# Revit family: QF_ELECTROLUXPROFESSIONAL_1LSNTD_WS6-11_E
name_source: partatom
category: Attrezzature speciali
units: mm (PartAtom-declared; Revit-internal decimal feet)

## family parameters
Basato su piano di lavoro = No
Condiviso = No
Punto di calcolo locali = No
Quota connettore circolare = Usa diametro
Sempre verticale = Sì
Taglio con vuoti quando caricato = No
Tipo di parte = Normale

## types (17) — shared parameters
Depth = 697 mm  [stored 2.28675 ft]
Depth Actual = 700 mm  [stored 2.29659 ft]
Height = 1218.8 mm  [stored 3.99869 ft]
Height Actual = 1220 mm  [stored 4.00262 ft]
Latent Heat Output = 0.0
Length Actual = 720 mm  [stored 2.3622 ft]
Modello = WS6-11
Produttore = Electrolux Professional
Sensible Heat Output = 0.0
URL = www.electroluxprofessional.com
Weight = 152
Width = 720 mm  [stored 2.3622 ft]
zero-valued in all types: Gas KW, Prospetto di default, Steam Pounds per Hour

## per-type parameters (varying)
| type | Cycle | Descrizione | Item Number | Phase | Volts | Watts |
| 9867730227 | 50 Hz | WASHER WS6-11 11KG EL 10KW 380-415/50/3 COMPASS PRO 6G07 ML 2xWATER POWDER+5xLIQ. VALV.OPEN SST/SILVER 2.I/O QC TRAFO DI | 1L0H2N | 3 | 415 V | 8800 W |
| 9867730113 | 50 Hz | WASHER WS6-11 11KG MOP 10KW 380-415/50/3N COMPASS PRO 6F01 ML 2xWATER POWDER+ED EL.VALV.OPEN SST DISCON. STOP LID | 1L0GCV | 3 | 415 V | 8800 W |
| 9867730064 | 50 Hz | WASHER WS6-11 11KG EL 10KW 380-415/50/3N COMPASS PRO 6H01 ML 2xWATER POWDER+5xLIQ. VALV.OPEN SILVER 2.I/O DISCON. STOP | 1LSP5E | 3 | 415 V | 10400 W |
| 9867730112 | 50 Hz | WASHER WS6-11 11KG EL 10KW 380-415/50/3N COMPASS PRO 6G01 ML 2xWATER POWDER+5xLIQ. VALV.OPEN SILVER 2.I/O DISCON. STOP | 1L0GCU | 3 | 415 V | 8800 W |
| 9867730101 | 50 Hz | WASHER WS6-11 11KG NO HEAT 220-240/50/1N COMPASS PRO 6G05 ML 2xWATER POWDER+5xLIQ. VALV.OPEN SST/SILVER 2.I/O DISCON. ST | 1L821N | 1 | 240 V | 800 W |
| 9867730196 | 50 Hz | WASHER WS6-11 11KG NO HEAT 200/50/60/3 COMPASS PRO 6L41 JP,EN 2xWATER 5xLIQ. VALV.OPEN SST/SILVER 2.I/O DISCON. | 1L0GXM | 3 | 200 V | 900 W |
| 9867730122 | 50 Hz | WASHER WS6-11 11KG MOP 10KW 380-400/220-230/50/3N/3 COMPASS PRO 6M14 ML 2xWATER POWDER+5xLIQ. EL.VALV.OPEN SILVER 2.I/O | 1LA1CA | 3 | 415 V | 10400 W |
| 9867730082 | 50 Hz | WASHER WS6-11 11KG NO HEAT 220-240/50/1N COMPASS PRO 6L01 ML 2xWATER POWDER+5xLIQ. VALV.OPEN SILVER EXT.PM. 2.I/O DISCON | 1LSP5M | 1 | 240 V | 800 W |
| 9867730145 | 60 Hz | WASHER WS6-11 11KG EL 10KW 220-230/60/1 COMPASS PRO 6G07 ML 2xWATER POWDER+5xLIQ. VALV.OPEN SST 2.I/O QC DISCON. STOP | 1LSPD4 | 1 | 240 V | 10400 W |
| 9867730165 | 60 Hz | WASHER WS6-11 11KG NO HEAT 208-240/60/1 COMPASS PRO 6L01 ML 2xWATER POWDER+5xLIQ. VALV.OPEN SILVER ELS-NETW. 2.I/O | 1L0GNC | 1 | 240 V | 800 W |
| 9867730176 | 50 Hz | WASHER WS6-11 11KG NO HEAT 220-240/50/1N COMPASS PRO 6L01 ML 2xWATER POWDER+5xLIQ. VALV.OPEN SILVER 2.I/O DISCON. | 1L826T | 1 | 240 V | 800 W |
| 9867730188 | 50 Hz | WASHER WS6-11 11KG NO HEAT 200/50/60/3 COMPASS PRO 6L41 JP,EN 2xWATER POWDER+5xLIQ. VALV.OPEN SILVER 2.I/O DISCON. | 1L827M | 3 | 200 V | 900 W |
| 9867730259 | 60 Hz | WASHER WS6-11 11KG NO HEAT 220-240/60/3 COMPASS PRO 6L01 ML 2xWATER POWDER VALV.OPEN SILVER DISCON. | 1LA26H | 3 | 220 V | 800 W |
| 9867730120 | 50 Hz | WASHER WS6-11 11KG NO HEAT 200/50/60/3 COMPASS PRO 6L41 JP,EN 2xWATER 5xLIQ. VALV.OPEN SILVER 2.I/O DISCON. | 1LSP8V | 3 | 200 V | 900 W |
| 9867730129 | 60 Hz | WASHER WS6-11 11KG NO HEAT 208-240/60/1 COMPASS PRO 6G01 ML 2xWATER POWDER+5xLIQ. VALV.CLOSED SILVER 2.I/O STOP | 1LSPA3 | 1 | 240 V | 800 W |
| 9867730144 | 60 Hz | WASHER WS6-11 11KG EL 10KW 440/60/3 COMPASS PRO 6G07 ML 2xWATER POWDER+5xLIQ. VALV.OPEN SST 2.I/O QC TRAFO DISCON. STOP | 1LSPCM | 3 | 440 V | 10500 W |
| 9867730224 | 60 Hz | WASHER WS6-11 11KG EL 7,5KW 440/60/3 COMPASS PRO 6G01 ML 2xWATER POWDER+ED VALV.OPEN SST/SILVER TRAFO DISCON. STOP | 1LSPSK | 3 | 440 V | 8000 W |

note: [stored X ft] marks values corroborated as IEEE doubles in the binary element streams (Revit-internal decimal feet)

## geometry (parser evidence)
native form markers: Sweep x4
no freeform markers — native parametric forms only
